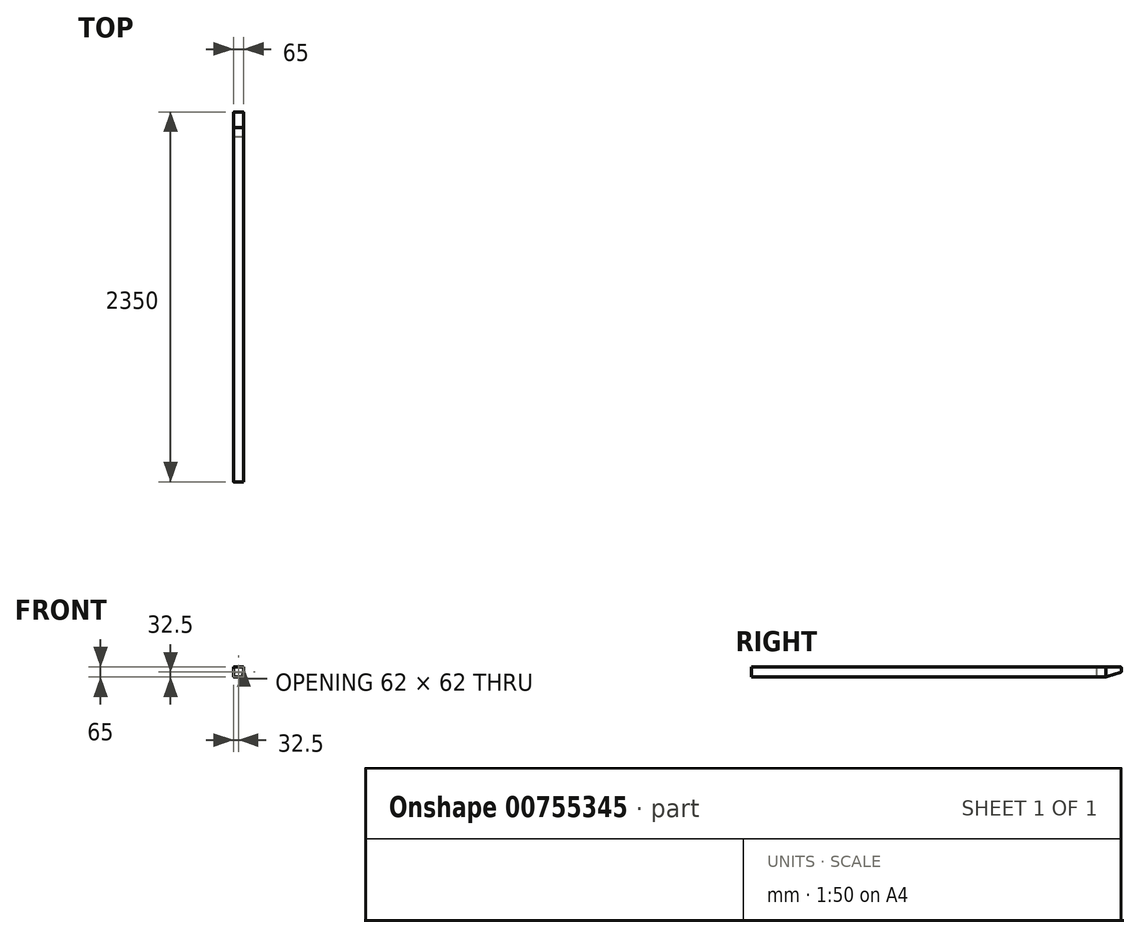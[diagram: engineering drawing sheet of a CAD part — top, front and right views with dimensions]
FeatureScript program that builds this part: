
annotation { "Feature Type Name" : "Feature", "Feature Type Description" : "" }
export const myFeature = defineFeature(function(context is Context, id is Id, definition is map)
    precondition{}
    {
        {
            var Q0;
            Q0=qCreatedBy(makeId("Front.planeOp"),FACE);
            var sketch = newSketch(context, id + "F0", { "sketchPlane" : qUnion([Q0])});
            skLineSegment(sketch, "E0.bottom", {"start": v(27.5, 32.5) * mm, "end": v(-27.5, 32.5) * mm});
            skLineSegment(sketch, "E0.top", {"start": v(27.5, -32.5) * mm, "end": v(-27.5, -32.5) * mm});
            skLineSegment(sketch, "E0.left", {"start": v(32.5, 27.5) * mm, "end": v(32.5, -27.5) * mm});
            skLineSegment(sketch, "E0.right", {"start": v(-32.5, 27.5) * mm, "end": v(-32.5, -27.5) * mm});
            skPoint(sketch, "E0.middle", {"position": v(0, 0) * mm});
            skPoint(sketch, "E1.visualSharp", {"position": v(-32.5, 32.5) * mm});
            skArc(sketch, "E1.filletArc", {"start": v(-27.5, 32.5) * mm, "mid": v(-31.04, 31.04) * mm, "end": v(-32.5, 27.5) * mm});
            skPoint(sketch, "E2.visualSharp", {"position": v(32.5, 32.5) * mm});
            skArc(sketch, "E2.filletArc", {"start": v(32.5, 27.5) * mm, "mid": v(31.04, 31.04) * mm, "end": v(27.5, 32.5) * mm});
            skPoint(sketch, "E3.visualSharp", {"position": v(32.5, -32.5) * mm});
            skArc(sketch, "E3.filletArc", {"start": v(27.5, -32.5) * mm, "mid": v(31.04, -31.04) * mm, "end": v(32.5, -27.5) * mm});
            skPoint(sketch, "E4.visualSharp", {"position": v(-32.5, -32.5) * mm});
            skArc(sketch, "E4.filletArc", {"start": v(-32.5, -27.5) * mm, "mid": v(-31.04, -31.04) * mm, "end": v(-27.5, -32.5) * mm});
            skPoint(sketch, "E5.visualSharp", {"position": v(-29.5, 29.5) * mm});
            skArc(sketch, "E6.0", {"start": v(31, 27.5) * mm, "mid": v(29.97, 29.97) * mm, "end": v(27.5, 31) * mm});
            skLineSegment(sketch, "E6.1", {"start": v(31, 27.5) * mm, "end": v(31, -27.5) * mm});
            skLineSegment(sketch, "E6.2", {"start": v(27.5, 31) * mm, "end": v(-27.5, 31) * mm});
            skArc(sketch, "E6.3", {"start": v(27.5, -31) * mm, "mid": v(29.97, -29.97) * mm, "end": v(31, -27.5) * mm});
            skArc(sketch, "E6.4", {"start": v(-27.5, 31) * mm, "mid": v(-29.97, 29.97) * mm, "end": v(-31, 27.5) * mm});
            skLineSegment(sketch, "E6.5", {"start": v(-31, 27.5) * mm, "end": v(-31, -27.5) * mm});
            skArc(sketch, "E6.6", {"start": v(-31, -27.5) * mm, "mid": v(-29.97, -29.97) * mm, "end": v(-27.5, -31) * mm});
            skLineSegment(sketch, "E6.7", {"start": v(27.5, -31) * mm, "end": v(-27.5, -31) * mm});
            skSolve(sketch);
        }
        {
            var Q0;
            Q0=makeQuery(id+"F0.imprint","IMPRINT",FACE,{"disambiguationData":[TD([[makeQuery(id+"F0.imprint","IMPRINT",EDGE,{"derivedFrom":sQuery(id+"F0.wireOp",EDGE,"E0.bottom")}),1.0]])]});
            extrude(context, id + "F1", {"entities" : qUnion([Q0]), "depth" : 2250 * mm, "offsetDistance" : 25 * mm});
        }
        {
            var Q0;
            Q0=makeQuery(id+"F0.imprint","IMPRINT",FACE,{"disambiguationData":[TD([[makeQuery(id+"F0.imprint","IMPRINT",EDGE,{"derivedFrom":sQuery(id+"F0.wireOp",EDGE,"E6.0")}),1.0]])]});
            extrude(context, id + "F2", {"entities" : qUnion([Q0]), "depth" : 120 * mm, "offsetDistance" : 25 * mm, "symmetric" : true});
        }
        {
            var Q0;
            Q0=makeQuery(id+"F2.opExtrude","CAP_FACE",FACE,{"disambiguationData":[OSD([sQuery(id+"F0.wireOp",EDGE,"E6.0"),sQuery(id+"F0.wireOp",EDGE,"E6.1"),sQuery(id+"F0.wireOp",EDGE,"E6.2"),sQuery(id+"F0.wireOp",EDGE,"E6.3"),sQuery(id+"F0.wireOp",EDGE,"E6.4"),sQuery(id+"F0.wireOp",EDGE,"E6.5"),sQuery(id+"F0.wireOp",EDGE,"E6.6"),sQuery(id+"F0.wireOp",EDGE,"E6.7")])],"isStart":true});
            extrude(context, id + "F3", {"entities" : qUnion([Q0]), "operationType" : NewBodyOperationType.ADD, "depth" : 40 * mm, "offsetDistance" : 25 * mm});
        }
        {
            var Q0;
            {var subQ0=sQuery(id+"F0.wireOp",EDGE,"E6.1");Q0=makeQuery(id+"F3.boolean.opBoolean","MERGE",FACE,{"derivedFrom":[makeQuery(id+"F2.opExtrude","SWEPT_FACE",FACE,{"disambiguationData":[OSD([subQ0])]}),makeQuery(id+"F3.opExtrude","SWEPT_FACE",FACE,{"disambiguationData":[OSD([subQ0])]})]});}
            var sketch = newSketch(context, id + "F4", { "sketchPlane" : qUnion([Q0])});
            skPoint(sketch, "E7.0", {"position": v(100, 0) * mm});
            skPoint(sketch, "E8.0", {"position": v(0, -31) * mm});
            skLineSegment(sketch, "E9", {"start": v(0, -31) * mm, "end": v(100, 0) * mm});
            skLineSegment(sketch, "E10", {"start": v(100, 0) * mm, "end": v(100, -31) * mm});
            skLineSegment(sketch, "E11", {"start": v(100, -31) * mm, "end": v(0, -31) * mm});
            skSolve(sketch);
        }
        {
            var Q0;
            {var subQ0=sQuery(id+"F4.wireOp",EDGE,"E11");Q0=makeQuery(id+"F4.imprint","IMPRINT",FACE,{"disambiguationData":[TD([[makeQuery(id+"F4.imprint","IMPRINT",EDGE,{"derivedFrom":subQ0}),-1.0]])]});}
            var Q1;
            {var subQ0=sQuery(id+"F4.wireOp",EDGE,"E10");var subQ1=sQuery(id+"F4.wireOp",EDGE,"E9");var subQ2=sQuery(id+"F0.wireOp",EDGE,"E6.1");var subQ3=makeQuery(id+"F4.imprint","INTERSECT",VERTEX,{"derivedFrom":[makeQuery(id+"F3.opExtrude","CAP_EDGE",EDGE,{"disambiguationData":[OSD([subQ2])],"isStart":false}),subQ1,subQ0]});Q1=makeQuery(id+"F4.imprint","IMPRINT",FACE,{"disambiguationData":[TD([[makeQuery(id+"F4.imprint","IMPRINT",EDGE,{"disambiguationData":[TD([[subQ3,1.0]])],"derivedFrom":subQ1}),-1.0]])]});}
            extrude(context, id + "F5", {"entities" : qUnion([Q0, Q1]), "operationType" : NewBodyOperationType.REMOVE, "endBound" : BoundingType.THROUGH_ALL, "oppositeDirection" : true, "depth" : 25 * mm, "offsetDistance" : 25 * mm});
        }
        {
            var Q0;
            Q0=makeQuery(id+"F3.opExtrude","CAP_EDGE",EDGE,{"disambiguationData":[OSD([sQuery(id+"F0.wireOp",EDGE,"E6.2")])],"isStart":false});
            fillet(context, id + "F6", {"entities" : qUnion([Q0]), "radius" : 5 * mm, "tangentPropagation" : true, "allowEdgeOverflow" : false});
        }
    });
